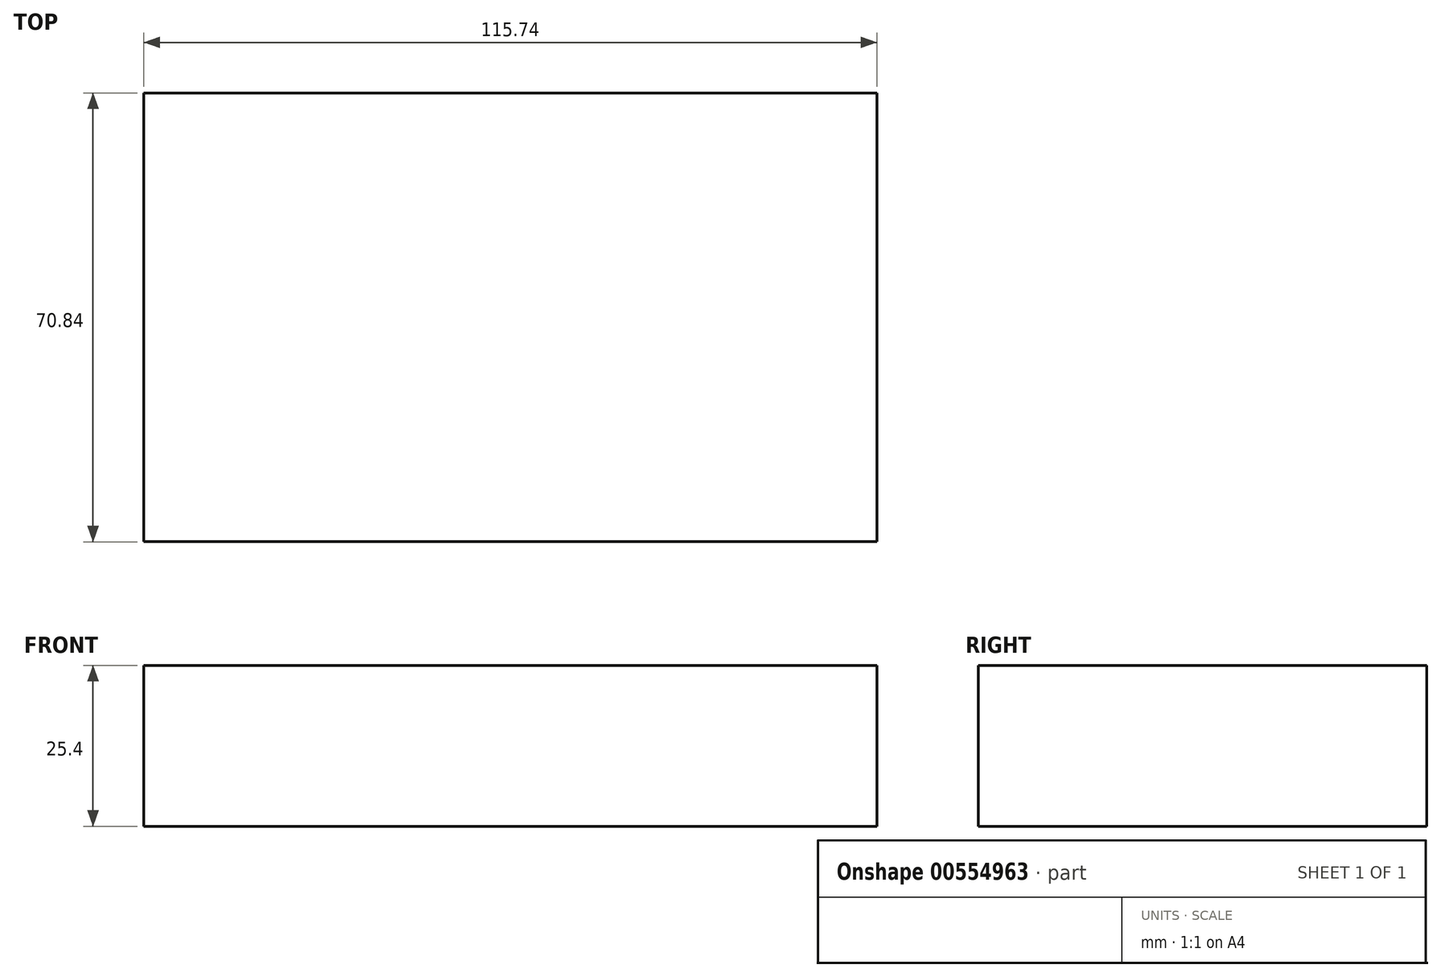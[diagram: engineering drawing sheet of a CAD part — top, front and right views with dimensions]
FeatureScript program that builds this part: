
annotation { "Feature Type Name" : "Feature", "Feature Type Description" : "" }
export const myFeature = defineFeature(function(context is Context, id is Id, definition is map)
    precondition{}
    {
        {
            var Q0;
            Q0=qCreatedBy(makeId("Top.planeOp"),FACE);
            var sketch = newSketch(context, id + "F0", { "sketchPlane" : qUnion([Q0])});
            skLineSegment(sketch, "E0.bottom", {"start": v(57.87, -35.42) * mm, "end": v(-57.87, -35.42) * mm});
            skLineSegment(sketch, "E0.top", {"start": v(57.87, 35.42) * mm, "end": v(-57.87, 35.42) * mm});
            skLineSegment(sketch, "E0.left", {"start": v(57.87, -35.42) * mm, "end": v(57.87, 35.42) * mm});
            skLineSegment(sketch, "E0.right", {"start": v(-57.87, -35.42) * mm, "end": v(-57.87, 35.42) * mm});
            skPoint(sketch, "E0.middle", {"position": v(0, 0) * mm});
            skSolve(sketch);
        }
        {
            var Q0;
            Q0 = qSketchRegion(id + "F0", true);
            extrude(context, id + "F1", {"entities" : qUnion([Q0]), "depth" : 25.4 * mm, "offsetDistance" : 25.4 * mm});
        }
    });
